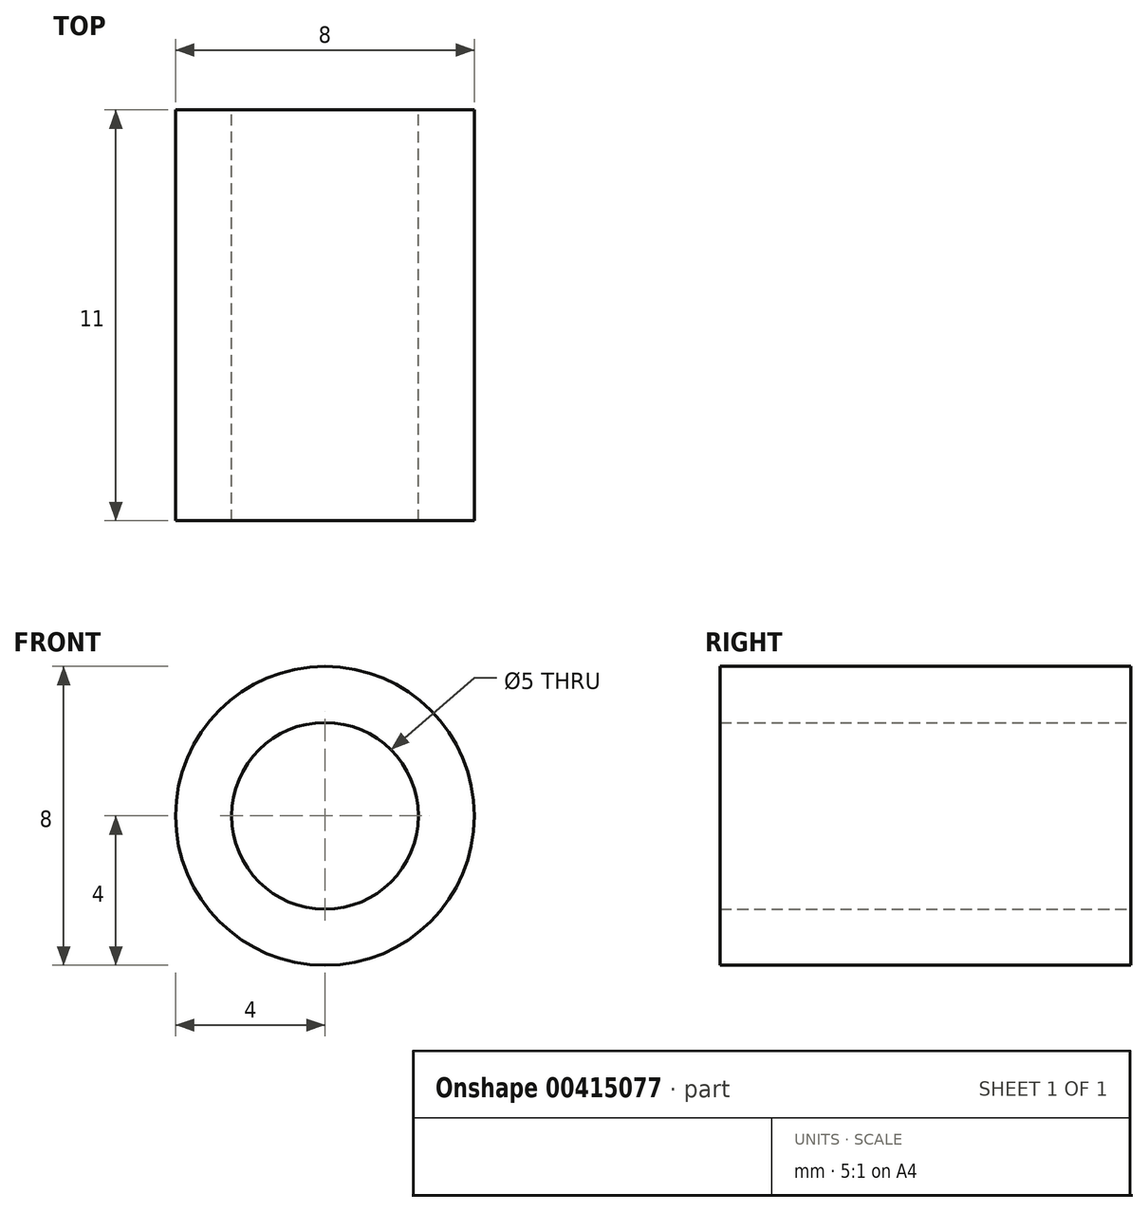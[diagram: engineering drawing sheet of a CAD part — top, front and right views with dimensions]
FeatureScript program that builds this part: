
annotation { "Feature Type Name" : "Feature", "Feature Type Description" : "" }
export const myFeature = defineFeature(function(context is Context, id is Id, definition is map)
    precondition{}
    {
        {
            var Q0;
            Q0=qCreatedBy(makeId("Front.planeOp"),FACE);
            var sketch = newSketch(context, id + "F0", { "sketchPlane" : qUnion([Q0])});
            skCircle(sketch, "E0", {"center": v(0, 0) * mm, "radius": 2.5 * mm});
            skCircle(sketch, "E1", {"center": v(0, 0) * mm, "radius": 4 * mm});
            skSolve(sketch);
        }
        {
            var Q0;
            Q0 = qSketchRegion(id + "F0", true);
            extrude(context, id + "F1", {"entities" : qUnion([Q0]), "depth" : 11 * mm});
        }
    });
